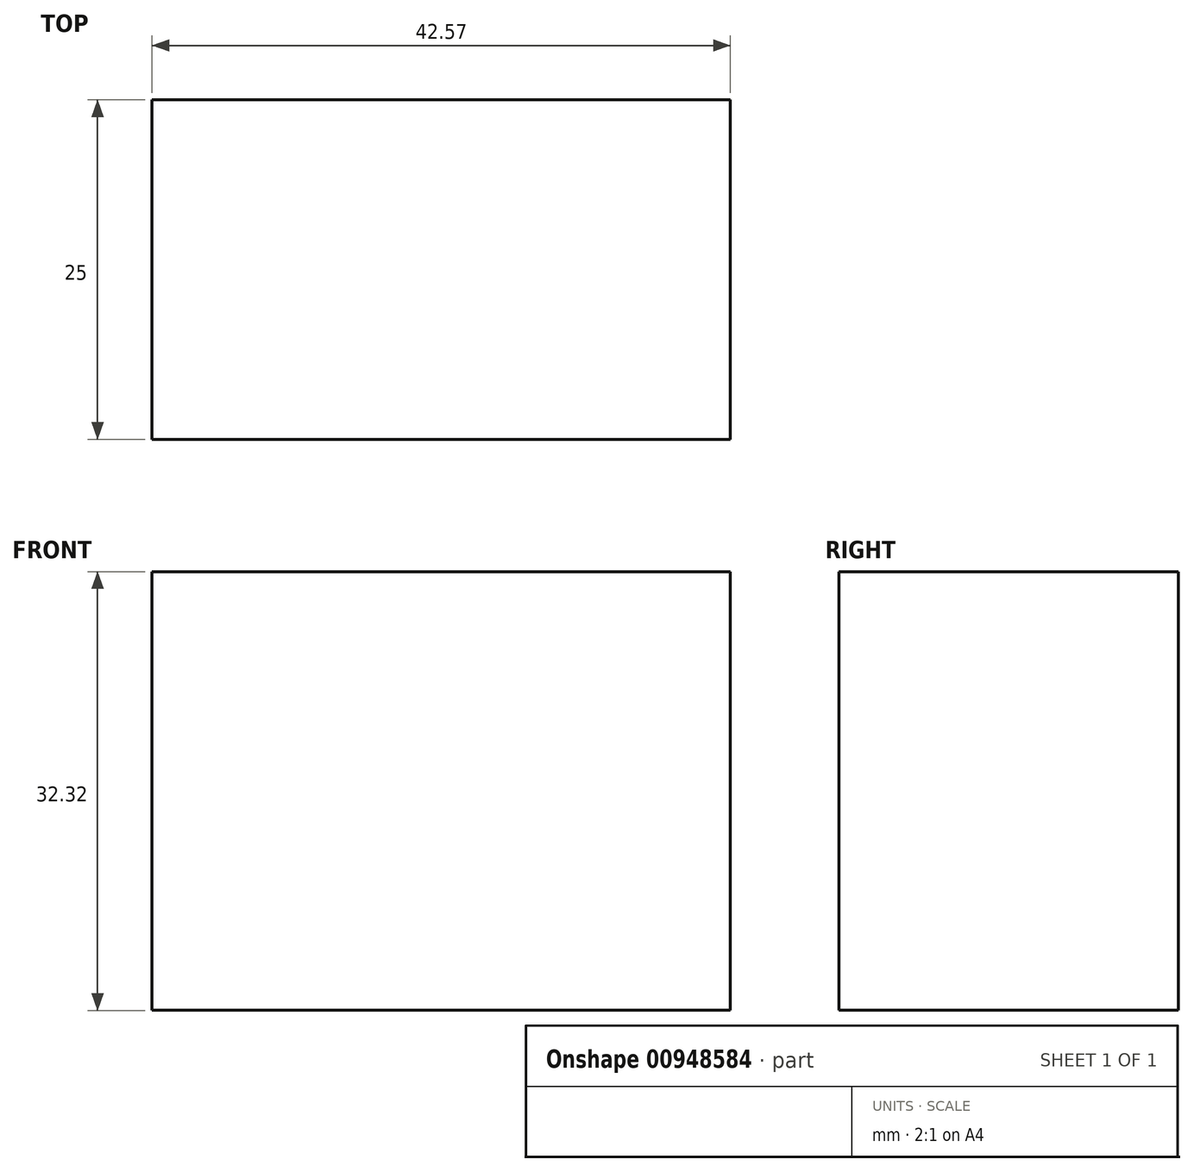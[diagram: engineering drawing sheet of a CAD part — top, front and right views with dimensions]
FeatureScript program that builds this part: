
annotation { "Feature Type Name" : "Feature", "Feature Type Description" : "" }
export const myFeature = defineFeature(function(context is Context, id is Id, definition is map)
    precondition{}
    {
        {
            var Q0;
            Q0=qCreatedBy(makeId("Front.planeOp"),FACE);
            var sketch = newSketch(context, id + "F0", { "sketchPlane" : qUnion([Q0])});
            skLineSegment(sketch, "E0.bottom", {"start": v(23.38, 40.5) * mm, "end": v(65.95, 40.5) * mm});
            skLineSegment(sketch, "E0.top", {"start": v(23.38, 8.2) * mm, "end": v(65.95, 8.2) * mm});
            skLineSegment(sketch, "E0.left", {"start": v(23.38, 40.5) * mm, "end": v(23.38, 8.2) * mm});
            skLineSegment(sketch, "E0.right", {"start": v(65.95, 40.5) * mm, "end": v(65.95, 8.2) * mm});
            skSolve(sketch);
        }
        {
            var Q0;
            Q0 = qSketchRegion(id + "F0", true);
            extrude(context, id + "F1", {"entities" : qUnion([Q0]), "depth" : 25 * mm, "offsetDistance" : 25 * mm});
        }
    });
